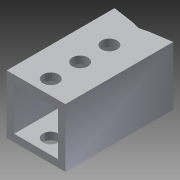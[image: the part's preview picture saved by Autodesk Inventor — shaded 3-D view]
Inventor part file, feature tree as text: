
AUTODESK INVENTOR PART (.ipt)
format: ipt  version: 2013 (Build 170138000, 138)  size: 153,600 bytes
history: native  units: in
note: dims shown in document units (in); Inventor stores cm internally (conversion verified against a paired STEP export)
features: extrude x6, sketch x5
ambient origin geometry x8: Origin, YZ Plane, XZ Plane, XY Plane, X Axis, Y Axis, Z Axis, Center Point
bodies: Solid1 (feature_tree)
feature tree (11):
  extrude  "Extrusion1"  Depth=1.0in
  extrude  "Extrusion2"  Depth=2.85in TaperAngle=0.0deg
  extrude  "Extrusion3"  Depth=0.075in
  extrude  "Extrusion4"  Depth=0.25in
  extrude  "Extrusion5"  Depth=1.1811in
  extrude  "Extrusion6"  Depth=1.0in TaperAngle=0.0deg
  sketch  "Sketch1"  dims[d2=1.0in d4=1.0in]
  sketch  "Sketch3"  dims[d5=0.125in d6=2.85in d7=0.0in]
  sketch  "Sketch4"  dims[d8=0.075in d9=0.075in]
  sketch  "Sketch5"  dims[d10=1.0in d11=0.0in d12=0.25in]
  sketch  "Sketch8"  dims[d13=0.266in d14=1.1811in d16=0.5in d17=0.3937in d19=1.0in d21=1.0in d22=0.0in d23=1.0in d24=90.0deg d25=1.0in d26=90.0deg d27=1.0in d28=0.0in d29=1.0in d30=0.0in d31=1.0in d32=0.0in]
